# Revit family: E438
name_source: partatom
category: Communication Devices
revit_build: Autodesk Revit 2018 (Build: 20170223_1515(x64)
units: mm (PartAtom-declared; Revit-internal decimal feet)

## family parameters
Always vertical = Yes
Cut with Voids When Loaded = No
Maintain Annotation Orientation = No
Part Type = Normal
Room Calculation Point = No
Round Connector Dimension = Use Diameter
Shared = No
Work Plane-Based = No

## types (2) — shared parameters
CONNECTIVITY- Analog = VGA (mini 15pin D-SUB) - Component VGA share (D-SUB) - Composite (mini jack 3.5mm)
CONNECTIVITY- Audio = Audio Mini Jack 3.5mm
CONNECTIVITY- Audio2 = SPDIF / Audio Mini Jack 3.5mm (for headphones)
CONNECTIVITY- Digital = HDMI x3 (2.0)*
CONNECTIVITY- External Control = LAN, RS232C**
CONNECTIVITY- Input Terminals = -
CONNECTIVITY- Output Terminals = -
CONNECTIVITY- Speaker Rating = Integrated 10W x 2
CONNECTIVITY- Tuner = Integrated ATSC (8-VSB, Clear-QAM)/NTSC Coaxial Tuner
CONNECTIVITY- USB Type-A port = USB Media Player (5V/500 mA)
CONNECTIVITY- USB Type-C port = Power Supply (5V/3A)
ENVIRONMENTAL CONDITIONS- Operating Altitude = 0 - 3000m (0 - 9843ft)
ENVIRONMENTAL CONDITIONS- Operating Humidity = 20-80% (without condensation)
ENVIRONMENTAL CONDITIONS- Operating Temperature = 0 - 40 °C / 32 - 104 °F
LCD MODULE- Aspect Ratio = 16:9
LCD MODULE- Brightness (Typical/Minimum) = 350 cd/m² / 320 cd/m²
LCD MODULE- Contrast Ratio (typical) = 8,000:1 (Out of the box conditions, local dimming ON)
LCD MODULE- Displayable Colors = Over 1.07 Billion
LCD MODULE- Native Resolution = 3480 x 2160
LCD MODULE- Orientation = Landscape
LCD MODULE- Panel Technology = IPS
LCD MODULE- Viewable Image Size = 42.5"
LCD MODULE- Viewing Angle (typical) = 178° Vert., 178° Hor. (89U/89D/89L/89R)
Manufacturer = NEC Display Solutions
Model = E438
PHYSICAL SPECS- Bezel Width (L/R, T/B) = 13.0mm/13.0mm/13.0mm/14.4mm
PHYSICAL SPECS- Net Dimensions (Without Stand W x H x D) = 38.3 x 22.04 x 2.80 in. (970.2 x 559.8 x 71.0 mm)
PHYSICAL SPECS- Net Weight (Without Stand W x H x D) = 10.2kg / 22.4lbs.
PHYSICAL SPECS- VESA Hole Configuration = 400 x 600
POWER CONSUMPTION- Current Rating = 1.5A - 0.6A @ 100V - 240V
POWER CONSUMPTION- Network Standby = 2W
POWER CONSUMPTION- On (Typ/Max Brightness/All Max) = 72W/84W/130W
POWER CONSUMPTION- Standby = 0.5W
URL = www.necdisplay.com

## per-type parameters (varying)
| type | Table Stand |
| E438 with Stand | Yes |
| E438 no Stand | No |

## geometry (parser evidence)
native form markers: Sweep x2
no freeform markers — native parametric forms only
